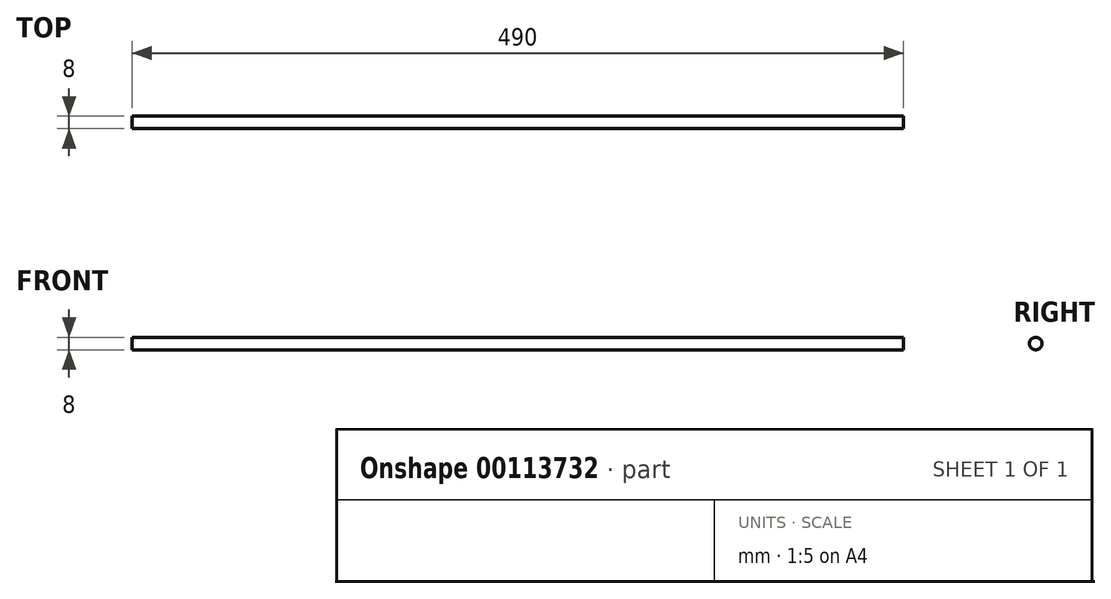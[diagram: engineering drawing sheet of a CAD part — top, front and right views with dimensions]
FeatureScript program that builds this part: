
annotation { "Feature Type Name" : "Feature", "Feature Type Description" : "" }
export const myFeature = defineFeature(function(context is Context, id is Id, definition is map)
    precondition{}
    {
        {
            var Q0;
            Q0=qCreatedBy(makeId("Right.planeOp"),FACE);
            var sketch = newSketch(context, id + "F0", { "sketchPlane" : qUnion([Q0])});
            skCircle(sketch, "E0", {"center": v(0, 0) * mm, "radius": 4 * mm});
            skSolve(sketch);
        }
        {
            var Q0;
            Q0=makeQuery(id+"F0.imprint","IMPRINT",FACE,{"disambiguationData":[TD([[makeQuery(id+"F0.imprint","IMPRINT",EDGE,{"derivedFrom":sQuery(id+"F0.wireOp",EDGE,"E0")}),1.0]])]});
            extrude(context, id + "F1", {"entities" : qUnion([Q0]), "depth" : 490 * mm});
        }
    });
